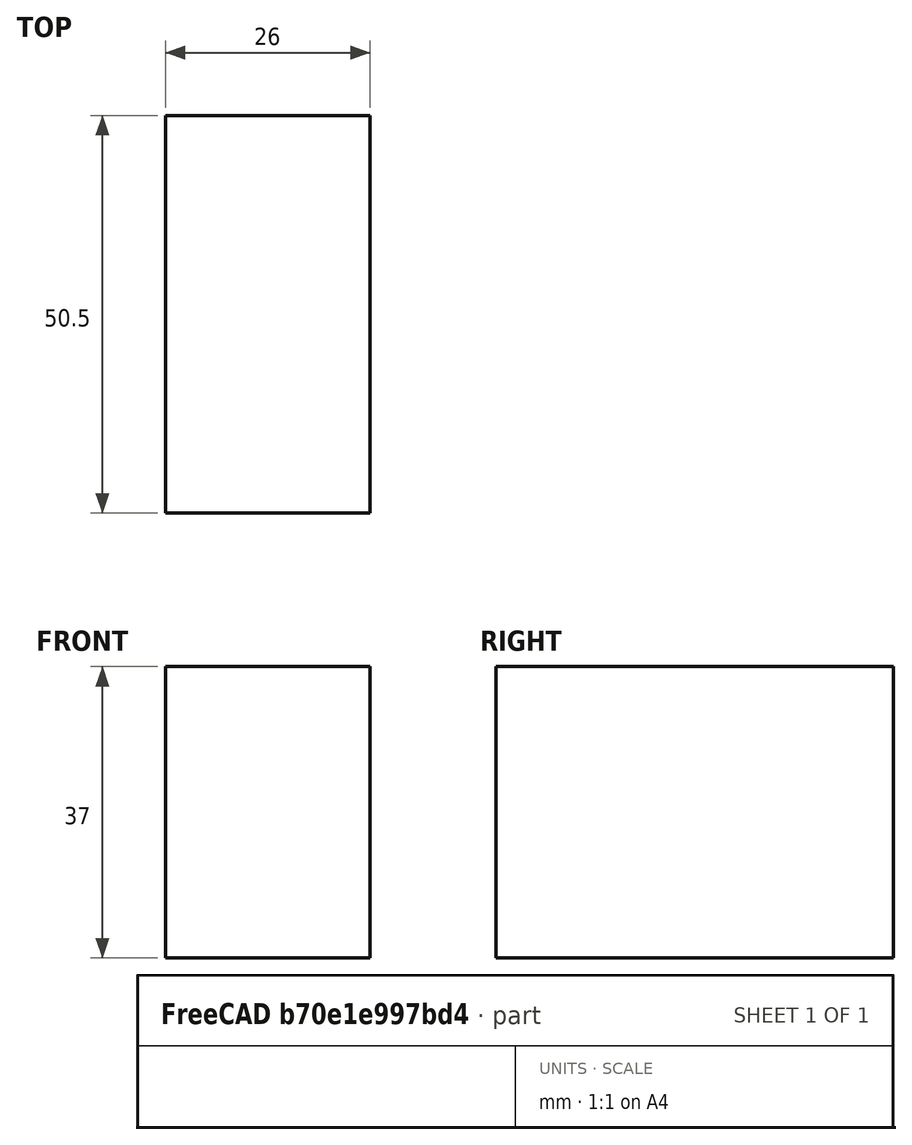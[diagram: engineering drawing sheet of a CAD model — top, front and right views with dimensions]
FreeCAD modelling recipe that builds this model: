
FCSTD DOCUMENT  (FreeCAD 0.19R24276 (Git))
Label: werit-terminal-block-114-12510000-00
License: All rights reserved
LicenseURL: http://en.wikipedia.org/wiki/All_rights_reserved
objects: Sketcher::SketchObject×1, PartDesign::Pad×1, PartDesign::Body×1
note: 4 computed .brp shape members not serialized (recipe doc carries the construction recipe); baked Part::Feature solids carry a one-line shape summary decoded from their .brp

FEATURE [Sketcher::SketchObject] Sketch
  FullyConstrained = true
  MapMode = 5
  Support = -> [XY_Plane]
  sketch-geometry (4):
    g0: LineSegment StartX=-13 StartY=25.25 StartZ=0 EndX=13 EndY=25.25 EndZ=0
    g1: LineSegment StartX=13 StartY=25.25 StartZ=0 EndX=13 EndY=-25.25 EndZ=0
    g2: LineSegment StartX=13 StartY=-25.25 StartZ=0 EndX=-13 EndY=-25.25 EndZ=0
    g3: LineSegment StartX=-13 StartY=-25.25 StartZ=0 EndX=-13 EndY=25.25 EndZ=0
  constraints (12):
    c: Coincident(g0,g1)
    c: Coincident(g1,g2)
    c: Coincident(g2,g3)
    c: Coincident(g3,g0)
    c: Horizontal(g0)
    c: Horizontal(g2)
    c: Vertical(g1)
    c: Vertical(g3)
    c: DistanceY(g-1,g0) = 25.25
    c: DistanceY(g2,g-1) = 25.25
    c: DistanceX(g0,g-1) = 13
    c: DistanceX(g-1,g0) = 13
FEATURE [PartDesign::Pad] Pad
  Direction = (1,1,1)
  Length = 37
  Length2 = 100
  Profile = -> Sketch
  Type = 0
FEATURE [PartDesign::Body] Body
  Group = -> [Sketch,Pad]
  Origin = -> Origin
  Tip = -> Pad
